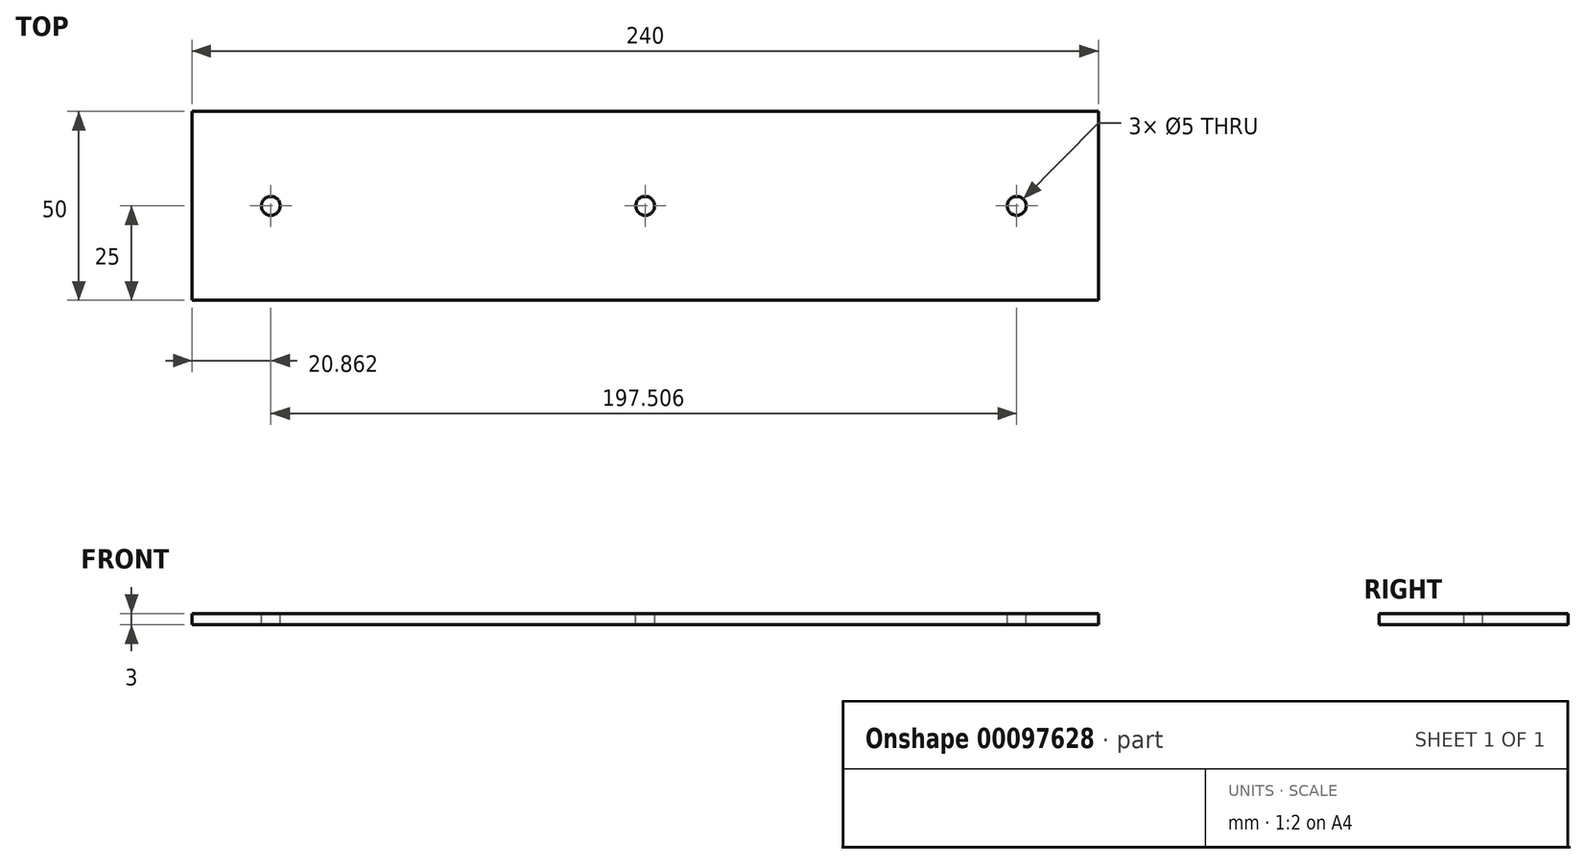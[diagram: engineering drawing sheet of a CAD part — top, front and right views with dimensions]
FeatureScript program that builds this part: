
annotation { "Feature Type Name" : "Feature", "Feature Type Description" : "" }
export const myFeature = defineFeature(function(context is Context, id is Id, definition is map)
    precondition{}
    {
        {
            var Q0;
            Q0=qCreatedBy(makeId("Top.planeOp"),FACE);
            var sketch = newSketch(context, id + "F0", { "sketchPlane" : qUnion([Q0])});
            skLineSegment(sketch, "E0.bottom", {"start": v(120, -25) * mm, "end": v(-120, -25) * mm});
            skLineSegment(sketch, "E0.top", {"start": v(120, 25) * mm, "end": v(-120, 25) * mm});
            skLineSegment(sketch, "E0.left", {"start": v(120, -25) * mm, "end": v(120, 25) * mm});
            skLineSegment(sketch, "E0.right", {"start": v(-120, -25) * mm, "end": v(-120, 25) * mm});
            skPoint(sketch, "E0.middle", {"position": v(0, 0) * mm});
            skSolve(sketch);
        }
        {
            var Q0;
            Q0 = qSketchRegion(id + "F0", true);
            extrude(context, id + "F1", {"entities" : qUnion([Q0]), "depth" : 3 * mm});
        }
        {
            var Q0;
            Q0=makeQuery(id+"F1.opExtrude","CAP_FACE",FACE,{"disambiguationData":[OSD([sQuery(id+"F0.wireOp",EDGE,"E0.bottom"),sQuery(id+"F0.wireOp",EDGE,"E0.top"),sQuery(id+"F0.wireOp",EDGE,"E0.left"),sQuery(id+"F0.wireOp",EDGE,"E0.right")])],"isStart":false});
            var sketch = newSketch(context, id + "F2", { "sketchPlane" : qUnion([Q0])});
            skLineSegment(sketch, "E1", {"start": v(-115.31, 0) * mm, "end": v(120, 0) * mm, "construction": true});
            skPoint(sketch, "E1.startSnap0", {"position": v(-120, 0) * mm});
            skLineSegment(sketch, "E2.0", {"start": v(-99, -25) * mm, "end": v(-99, 25) * mm, "construction": true});
            skLineSegment(sketch, "E3.0", {"start": v(99, -25) * mm, "end": v(99, 25) * mm, "construction": true});
            skLineSegment(sketch, "E4", {"start": v(0, 0) * mm, "end": v(0, 25) * mm, "construction": true});
            skSolve(sketch);
        }
        {
            var Q0;
            Q0=makeQuery(id+"F2.imprint","IMPRINT",FACE,{"disambiguationData":[TD([[makeQuery(id+"F2.imprint","IMPRINT",EDGE,{"derivedFrom":makeQuery(id+"F1.opExtrude","CAP_EDGE",EDGE,{"disambiguationData":[OSD([sQuery(id+"F0.wireOp",EDGE,"E0.bottom")])],"isStart":false})}),-1.0]])]});
            var sketch = newSketch(context, id + "F3", { "sketchPlane" : qUnion([Q0])});
            skCircle(sketch, "E5", {"center": v(-99.14, 0) * mm, "radius": 2.5 * mm});
            skSolve(sketch);
        }
        {
            var Q0;
            Q0=sQuery(id+"F3.wireOp",VERTEX,"E5.center");
            var Q1;
            Q1=makeQuery(id+"F1.opExtrude","SWEPT_BODY",BODY,{"disambiguationData":[OSD([sQuery(id+"F0.wireOp",EDGE,"E0.bottom"),sQuery(id+"F0.wireOp",EDGE,"E0.top"),sQuery(id+"F0.wireOp",EDGE,"E0.left"),sQuery(id+"F0.wireOp",EDGE,"E0.right")])]});
            hole(context, id + "F4", {"style" : HoleStyle.SIMPLE, "endStyle" : HoleEndStyle.THROUGH, "holeDiameter" : 5 * mm, "locations" : qUnion([Q0]), "scope" : qUnion([Q1]), "isTappedThrough" : true});
        }
        {
            var Q0;
            Q0=sQuery(id+"F2.wireOp",VERTEX,"E4.start");
            var Q1;
            Q1=makeQuery(id+"F1.opExtrude","SWEPT_BODY",BODY,{"disambiguationData":[OSD([sQuery(id+"F0.wireOp",EDGE,"E0.bottom"),sQuery(id+"F0.wireOp",EDGE,"E0.top"),sQuery(id+"F0.wireOp",EDGE,"E0.left"),sQuery(id+"F0.wireOp",EDGE,"E0.right")])]});
            hole(context, id + "F5", {"style" : HoleStyle.SIMPLE, "endStyle" : HoleEndStyle.THROUGH, "holeDiameter" : 5 * mm, "locations" : qUnion([Q0]), "scope" : qUnion([Q1]), "isTappedThrough" : true});
        }
        {
            var Q0;
            Q0=makeQuery(id+"F3.imprint","IMPRINT",FACE,{"disambiguationData":[TD([[makeQuery(id+"F3.imprint","IMPRINT",EDGE,{"derivedFrom":sQuery(id+"F3.wireOp",EDGE,"E5")}),-1.0]])]});
            var sketch = newSketch(context, id + "F6", { "sketchPlane" : qUnion([Q0])});
            skCircle(sketch, "E6", {"center": v(98.37, 0) * mm, "radius": 2.5 * mm});
            skSolve(sketch);
        }
        {
            var Q0;
            Q0=sQuery(id+"F6.wireOp",VERTEX,"E6.center");
            var Q1;
            Q1=makeQuery(id+"F1.opExtrude","SWEPT_BODY",BODY,{"disambiguationData":[OSD([sQuery(id+"F0.wireOp",EDGE,"E0.bottom"),sQuery(id+"F0.wireOp",EDGE,"E0.top"),sQuery(id+"F0.wireOp",EDGE,"E0.left"),sQuery(id+"F0.wireOp",EDGE,"E0.right")])]});
            hole(context, id + "F7", {"style" : HoleStyle.SIMPLE, "endStyle" : HoleEndStyle.THROUGH, "holeDiameter" : 5 * mm, "locations" : qUnion([Q0]), "scope" : qUnion([Q1]), "isTappedThrough" : true});
        }
    });
